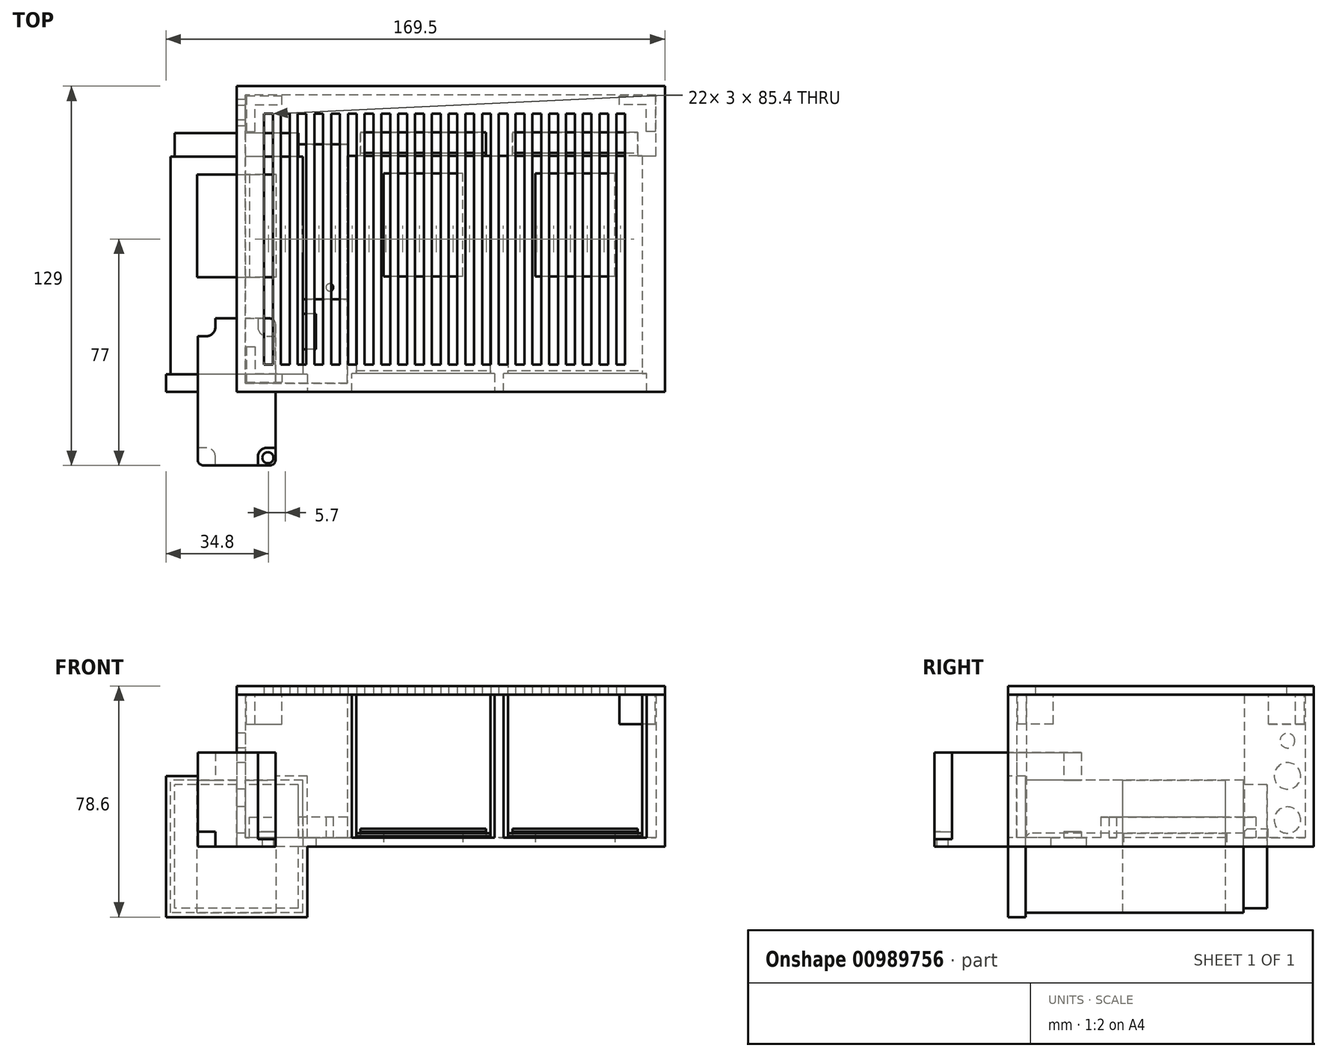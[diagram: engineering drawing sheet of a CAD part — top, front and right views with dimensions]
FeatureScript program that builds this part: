
annotation { "Feature Type Name" : "Feature", "Feature Type Description" : "" }
export const myFeature = defineFeature(function(context is Context, id is Id, definition is map)
    precondition{}
    {
        {
            assignVariable(context, id + "F0", {"name" : "panel_width", "anyValue" : 48 * mm});
        }
        {
            assignVariable(context, id + "F1", {"name" : "panel_depth", "anyValue" : 6 * mm});
        }
        {
            assignVariable(context, id + "F2", {"name" : "body_width", "anyValue" : 45 * mm});
        }
        {
            assignVariable(context, id + "F3", {"name" : "body_depth", "anyValue" : 74 * mm});
        }
        {
            assignVariable(context, id + "F4", {"name" : "connector_width", "anyValue" : 42 * mm});
        }
        {
            assignVariable(context, id + "F5", {"name" : "connector_depth", "anyValue" : 8 * mm});
        }
        {
            assignVariable(context, id + "F6", {"name" : "tol", "anyValue" : 0.3 * mm});
        }
        {
            assignVariable(context, id + "F7", {"name" : "eltako_height", "anyValue" : 32 * mm});
        }
        {
            assignVariable(context, id + "F8", {"name" : "eltako_h1", "anyValue" : 2.5 * mm});
        }
        {
            assignVariable(context, id + "F9", {"name" : "eltako_h2", "anyValue" : 5 * mm});
        }
        {
            assignVariable(context, id + "F10", {"name" : "wt", "anyValue" : 3 * mm});
        }
        {
            var Q0;
            Q0=qCreatedBy(makeId("Front.planeOp"),FACE);
            var sketch = newSketch(context, id + "F11", { "sketchPlane" : qUnion([Q0])});
            skLineSegment(sketch, "E0.bottom", {"start": v(24, -24) * mm, "end": v(-24, -24) * mm});
            skLineSegment(sketch, "E0.top", {"start": v(24, 24) * mm, "end": v(-24, 24) * mm});
            skLineSegment(sketch, "E0.left", {"start": v(24, -24) * mm, "end": v(24, 24) * mm});
            skLineSegment(sketch, "E0.right", {"start": v(-24, -24) * mm, "end": v(-24, 24) * mm});
            skPoint(sketch, "E0.middle", {"position": v(0, 0) * mm});
            skLineSegment(sketch, "E1.bottom", {"start": v(22.5, -22.5) * mm, "end": v(-22.5, -22.5) * mm});
            skLineSegment(sketch, "E1.top", {"start": v(22.5, 22.5) * mm, "end": v(-22.5, 22.5) * mm});
            skLineSegment(sketch, "E1.left", {"start": v(22.5, -22.5) * mm, "end": v(22.5, 22.5) * mm});
            skLineSegment(sketch, "E1.right", {"start": v(-22.5, -22.5) * mm, "end": v(-22.5, 22.5) * mm});
            skLineSegment(sketch, "E2.bottom", {"start": v(21, -21) * mm, "end": v(-21, -21) * mm});
            skLineSegment(sketch, "E2.top", {"start": v(21, 21) * mm, "end": v(-21, 21) * mm});
            skLineSegment(sketch, "E2.left", {"start": v(21, -21) * mm, "end": v(21, 21) * mm});
            skLineSegment(sketch, "E2.right", {"start": v(-21, -21) * mm, "end": v(-21, 21) * mm});
            skSolve(sketch);
        }
        {
            var Q0;
            Q0=makeQuery(id+"F11.imprint","IMPRINT",FACE,{"disambiguationData":[TD([[makeQuery(id+"F11.imprint","IMPRINT",EDGE,{"derivedFrom":sQuery(id+"F11.wireOp",EDGE,"E2.bottom")}),-1.0]])]});
            extrude(context, id + "F12", {"entities" : qUnion([Q0]), "oppositeDirection" : true, "depth" : getVariable(context, 'panel_depth') + getVariable(context, 'body_depth') + getVariable(context, 'connector_depth'), "offsetDistance" : 25 * mm});
        }
        {
            var Q0;
            Q0=makeQuery(id+"F11.imprint","IMPRINT",FACE,{"disambiguationData":[TD([[makeQuery(id+"F11.imprint","IMPRINT",EDGE,{"derivedFrom":sQuery(id+"F11.wireOp",EDGE,"E1.bottom")}),-1.0]])]});
            extrude(context, id + "F13", {"entities" : qUnion([Q0]), "operationType" : NewBodyOperationType.ADD, "oppositeDirection" : true, "depth" : getVariable(context, 'panel_depth') + getVariable(context, 'body_depth'), "offsetDistance" : 25 * mm});
        }
        {
            var Q0;
            Q0=makeQuery(id+"F11.imprint","IMPRINT",FACE,{"disambiguationData":[TD([[makeQuery(id+"F11.imprint","IMPRINT",EDGE,{"derivedFrom":sQuery(id+"F11.wireOp",EDGE,"E0.bottom")}),-1.0]])]});
            extrude(context, id + "F14", {"entities" : qUnion([Q0]), "operationType" : NewBodyOperationType.ADD, "oppositeDirection" : true, "depth" : getVariable(context, 'panel_depth'), "offsetDistance" : 25 * mm});
        }
        {
            var Q0;
            Q0=makeQuery(id+"F13.opExtrude","SWEPT_FACE",FACE,{"disambiguationData":[OSD([sQuery(id+"F11.wireOp",EDGE,"E1.top")])]});
            var sketch = newSketch(context, id + "F15", { "sketchPlane" : qUnion([Q0])});
            skLineSegment(sketch, "E3.bottom", {"start": v(13.5, 39) * mm, "end": v(-13.5, 39) * mm});
            skLineSegment(sketch, "E3.top", {"start": v(13.5, 74) * mm, "end": v(-13.5, 74) * mm});
            skLineSegment(sketch, "E3.left", {"start": v(13.5, 39) * mm, "end": v(13.5, 74) * mm});
            skLineSegment(sketch, "E3.right", {"start": v(-13.5, 39) * mm, "end": v(-13.5, 74) * mm});
            skPoint(sketch, "E3.middle", {"position": v(0, 56.5) * mm});
            skSolve(sketch);
        }
        {
            var Q0;
            Q0=makeQuery(id+"F15.imprint","IMPRINT",FACE,{"disambiguationData":[TD([[makeQuery(id+"F15.imprint","IMPRINT",EDGE,{"derivedFrom":sQuery(id+"F15.wireOp",EDGE,"E3.bottom")}),-1.0]])]});
            var Q1;
            Q1=makeQuery(id+"F13.opExtrude","SWEPT_FACE",FACE,{"disambiguationData":[OSD([sQuery(id+"F11.wireOp",EDGE,"E1.bottom")])]});
            extrude(context, id + "F16", {"entities" : qUnion([Q0]), "operationType" : NewBodyOperationType.REMOVE, "endBound" : BoundingType.UP_TO_SURFACE, "oppositeDirection" : true, "depth" : 25 * mm, "endBoundEntityFace" : qUnion([Q1]), "offsetDistance" : 25 * mm});
        }
        {
            var Q0;
            Q0=qCreatedBy(makeId("Top.planeOp"),FACE);
            var sketch = newSketch(context, id + "F17", { "sketchPlane" : qUnion([Q0])});
            skLineSegment(sketch, "E4.bottom", {"start": v(11.25, -25) * mm, "end": v(-11.25, -25) * mm});
            skLineSegment(sketch, "E4.top", {"start": v(11.25, 25) * mm, "end": v(-11.25, 25) * mm});
            skLineSegment(sketch, "E4.left", {"start": v(13.25, -23) * mm, "end": v(13.25, 23) * mm});
            skLineSegment(sketch, "E4.right", {"start": v(-13.25, -23) * mm, "end": v(-13.25, 23) * mm});
            skPoint(sketch, "E4.middle", {"position": v(0, 0) * mm});
            skPoint(sketch, "E5.visualSharp", {"position": v(13.25, 25) * mm});
            skArc(sketch, "E5.filletArc", {"start": v(13.25, 23) * mm, "mid": v(12.66, 24.41) * mm, "end": v(11.25, 25) * mm});
            skPoint(sketch, "E6.visualSharp", {"position": v(13.25, -25) * mm});
            skArc(sketch, "E6.filletArc", {"start": v(11.25, -25) * mm, "mid": v(12.66, -24.41) * mm, "end": v(13.25, -23) * mm});
            skPoint(sketch, "E7.visualSharp", {"position": v(-13.25, -25) * mm});
            skArc(sketch, "E7.filletArc", {"start": v(-13.25, -23) * mm, "mid": v(-12.66, -24.41) * mm, "end": v(-11.25, -25) * mm});
            skPoint(sketch, "E8.visualSharp", {"position": v(-13.25, 25) * mm});
            skArc(sketch, "E8.filletArc", {"start": v(-11.25, 25) * mm, "mid": v(-12.66, 24.41) * mm, "end": v(-13.25, 23) * mm});
            skLineSegment(sketch, "E9", {"start": v(7.25, 25) * mm, "end": v(7.25, 22) * mm});
            skLineSegment(sketch, "E10", {"start": v(10.25, 19) * mm, "end": v(13.25, 19) * mm});
            skPoint(sketch, "E11.visualSharp", {"position": v(7.25, 19) * mm});
            skArc(sketch, "E11.filletArc", {"start": v(7.25, 22) * mm, "mid": v(8.13, 19.88) * mm, "end": v(10.25, 19) * mm});
            skLineSegment(sketch, "E12", {"start": v(-13.25, 0) * mm, "end": v(13.25, 0) * mm, "construction": true});
            skLineSegment(sketch, "E13", {"start": v(0, 25) * mm, "end": v(0, -25) * mm, "construction": true});
            skLineSegment(sketch, "E14.MirrorCS", {"start": v(-7.25, 25) * mm, "end": v(-7.25, 22) * mm});
            skArc(sketch, "E15.MirrorCS", {"start": v(-7.25, 22) * mm, "mid": v(-8.13, 19.88) * mm, "end": v(-10.25, 19) * mm});
            skLineSegment(sketch, "E16.MirrorCS", {"start": v(-10.25, 19) * mm, "end": v(-13.25, 19) * mm});
            skLineSegment(sketch, "E17.MirrorCS", {"start": v(-10.25, -19) * mm, "end": v(-13.25, -19) * mm});
            skArc(sketch, "E18.MirrorCS", {"start": v(-7.25, -22) * mm, "mid": v(-8.13, -19.88) * mm, "end": v(-10.25, -19) * mm});
            skLineSegment(sketch, "E19.MirrorCS", {"start": v(-7.25, -25) * mm, "end": v(-7.25, -22) * mm});
            skLineSegment(sketch, "E20.MirrorCS", {"start": v(7.25, -25) * mm, "end": v(7.25, -22) * mm});
            skArc(sketch, "E21.MirrorCS", {"start": v(7.25, -22) * mm, "mid": v(8.13, -19.88) * mm, "end": v(10.25, -19) * mm});
            skLineSegment(sketch, "E22.MirrorCS", {"start": v(10.25, -19) * mm, "end": v(13.25, -19) * mm});
            skCircle(sketch, "E23", {"center": v(10.61, -22.36) * mm, "radius": 1.9 * mm});
            skLineSegment(sketch, "E24", {"start": v(10.25, -22) * mm, "end": v(11.25, -23) * mm, "construction": true});
            skLineSegment(sketch, "E25", {"start": v(12.51, -22.36) * mm, "end": v(13.25, -22.36) * mm, "construction": true});
            skLineSegment(sketch, "E26", {"start": v(10.61, -24.26) * mm, "end": v(10.61, -25) * mm, "construction": true});
            skCircle(sketch, "E27.1.0", {"center": v(-10.61, 22.36) * mm, "radius": 1.9 * mm});
            skLineSegment(sketch, "E28", {"start": v(10.61, -22.36) * mm, "end": v(0, 0) * mm, "construction": true});
            skLineSegment(sketch, "E29", {"start": v(0, 0) * mm, "end": v(-10.61, 22.36) * mm, "construction": true});
            skLineSegment(sketch, "E30", {"start": v(-10.61, 22.36) * mm, "end": v(10.61, 22.36) * mm, "construction": true});
            skLineSegment(sketch, "E31", {"start": v(10.61, 22.36) * mm, "end": v(10.61, -22.36) * mm, "construction": true});
            skSolve(sketch);
        }
        {
            var Q0;
            {var subQ1=sQuery(id+"F17.wireOp",EDGE,"E5.filletArc");Q0=makeQuery(id+"F17.imprint","IMPRINT",FACE,{"disambiguationData":[TD([[makeQuery(id+"F17.imprint","IMPRINT",EDGE,{"derivedFrom":subQ1}),1.0]])]});}
            var Q1;
            {var subQ2=sQuery(id+"F17.wireOp",EDGE,"E9");Q1=makeQuery(id+"F17.imprint","IMPRINT",FACE,{"disambiguationData":[TD([[makeQuery(id+"F17.imprint","IMPRINT",EDGE,{"derivedFrom":subQ2}),-1.0]])]});}
            var Q2;
            {var subQ0=sQuery(id+"F17.wireOp",EDGE,"E7.filletArc");Q2=makeQuery(id+"F17.imprint","IMPRINT",FACE,{"disambiguationData":[TD([[makeQuery(id+"F17.imprint","IMPRINT",EDGE,{"derivedFrom":subQ0}),1.0]])]});}
            extrude(context, id + "F18", {"entities" : qUnion([Q0, Q1, Q2]), "depth" : getVariable(context, 'eltako_height'), "offsetDistance" : 25 * mm});
        }
        {
            var Q0;
            {var subQ0=sQuery(id+"F17.wireOp",EDGE,"E6.filletArc");Q0=makeQuery(id+"F17.imprint","IMPRINT",FACE,{"disambiguationData":[TD([[makeQuery(id+"F17.imprint","IMPRINT",EDGE,{"derivedFrom":subQ0}),1.0]])]});}
            var Q1;
            {var subQ1=sQuery(id+"F17.wireOp",EDGE,"E8.filletArc");Q1=makeQuery(id+"F17.imprint","IMPRINT",FACE,{"disambiguationData":[TD([[makeQuery(id+"F17.imprint","IMPRINT",EDGE,{"derivedFrom":subQ1}),1.0]])]});}
            extrude(context, id + "F19", {"entities" : qUnion([Q0, Q1]), "operationType" : NewBodyOperationType.ADD, "depth" : getVariable(context, 'eltako_h1'), "offsetDistance" : 25 * mm});
        }
        {
            var Q0;
            {var subQ1=sQuery(id+"F17.wireOp",EDGE,"E5.filletArc");Q0=makeQuery(id+"F17.imprint","IMPRINT",FACE,{"disambiguationData":[TD([[makeQuery(id+"F17.imprint","IMPRINT",EDGE,{"derivedFrom":subQ1}),1.0]])]});}
            var Q1;
            {var subQ0=sQuery(id+"F17.wireOp",EDGE,"E7.filletArc");Q1=makeQuery(id+"F17.imprint","IMPRINT",FACE,{"disambiguationData":[TD([[makeQuery(id+"F17.imprint","IMPRINT",EDGE,{"derivedFrom":subQ0}),1.0]])]});}
            extrude(context, id + "F20", {"entities" : qUnion([Q0, Q1]), "operationType" : NewBodyOperationType.REMOVE, "depth" : getVariable(context, 'eltako_h2'), "offsetDistance" : 25 * mm});
        }
        {
            var Q0;
            Q0=qCreatedBy(makeId("Top.planeOp"),FACE);
            var sketch = newSketch(context, id + "F21", { "sketchPlane" : qUnion([Q0])});
            skLineSegment(sketch, "E32", {"start": v(0, 0) * mm, "end": v(145.5, 0) * mm});
            skLineSegment(sketch, "E33", {"start": v(0, 0) * mm, "end": v(0, 104) * mm});
            skLineSegment(sketch, "E34", {"start": v(0, 104) * mm, "end": v(145.5, 104) * mm});
            skLineSegment(sketch, "E35", {"start": v(145.5, 104) * mm, "end": v(145.5, 0) * mm});
            skLineSegment(sketch, "E36.0", {"start": v(3, 101) * mm, "end": v(142.5, 101) * mm});
            skLineSegment(sketch, "E36.1", {"start": v(3, 3) * mm, "end": v(3, 101) * mm});
            skLineSegment(sketch, "E36.2", {"start": v(3, 3) * mm, "end": v(142.5, 3) * mm});
            skLineSegment(sketch, "E36.3", {"start": v(142.5, 101) * mm, "end": v(142.5, 3) * mm});
            skLineSegment(sketch, "E37", {"start": v(137.8, 80.3) * mm, "end": v(137.8, 6.3) * mm});
            skLineSegment(sketch, "E38", {"start": v(137.8, 6.3) * mm, "end": v(139.3, 6.3) * mm});
            skLineSegment(sketch, "E39", {"start": v(139.3, 6.3) * mm, "end": v(139.3, 0) * mm});
            skLineSegment(sketch, "E40", {"start": v(137.8, 80.3) * mm, "end": v(136.3, 80.3) * mm});
            skLineSegment(sketch, "E41", {"start": v(136.3, 80.3) * mm, "end": v(136.3, 88.3) * mm});
            skLineSegment(sketch, "E42", {"start": v(136.3, 88.3) * mm, "end": v(93.7, 88.3) * mm});
            skLineSegment(sketch, "E43", {"start": v(93.7, 88.3) * mm, "end": v(93.7, 80.3) * mm});
            skLineSegment(sketch, "E44", {"start": v(93.7, 80.3) * mm, "end": v(92.2, 80.3) * mm});
            skLineSegment(sketch, "E45", {"start": v(92.2, 80.3) * mm, "end": v(92.2, 6.3) * mm});
            skLineSegment(sketch, "E46", {"start": v(92.2, 6.3) * mm, "end": v(90.7, 6.3) * mm});
            skLineSegment(sketch, "E47", {"start": v(90.7, 6.3) * mm, "end": v(90.7, 0) * mm});
            skLineSegment(sketch, "E48", {"start": v(87.7, 0) * mm, "end": v(87.7, 6.3) * mm});
            skLineSegment(sketch, "E49", {"start": v(87.7, 6.3) * mm, "end": v(86.2, 6.3) * mm});
            skLineSegment(sketch, "E50", {"start": v(86.2, 6.3) * mm, "end": v(86.2, 80.3) * mm});
            skLineSegment(sketch, "E51", {"start": v(86.2, 80.3) * mm, "end": v(84.7, 80.3) * mm});
            skLineSegment(sketch, "E52", {"start": v(84.7, 80.3) * mm, "end": v(84.7, 88.3) * mm});
            skLineSegment(sketch, "E53", {"start": v(84.7, 88.3) * mm, "end": v(42.1, 88.3) * mm});
            skLineSegment(sketch, "E54", {"start": v(42.1, 88.3) * mm, "end": v(42.1, 80.3) * mm});
            skLineSegment(sketch, "E55", {"start": v(42.1, 80.3) * mm, "end": v(40.6, 80.3) * mm});
            skLineSegment(sketch, "E56", {"start": v(40.6, 80.3) * mm, "end": v(40.6, 6.3) * mm});
            skLineSegment(sketch, "E57", {"start": v(40.6, 6.3) * mm, "end": v(39.1, 6.3) * mm});
            skLineSegment(sketch, "E58", {"start": v(39.1, 6.3) * mm, "end": v(39.1, 0) * mm});
            skLineSegment(sketch, "E59", {"start": v(92.2, 6.3) * mm, "end": v(137.8, 6.3) * mm});
            skLineSegment(sketch, "E60", {"start": v(93.7, 80.3) * mm, "end": v(136.3, 80.3) * mm});
            skLineSegment(sketch, "E61", {"start": v(42.1, 80.3) * mm, "end": v(84.7, 80.3) * mm});
            skLineSegment(sketch, "E62", {"start": v(40.6, 6.3) * mm, "end": v(86.2, 6.3) * mm});
            skLineSegment(sketch, "E63.bottom", {"start": v(76.9, 39.3) * mm, "end": v(49.9, 39.3) * mm});
            skLineSegment(sketch, "E63.top", {"start": v(76.9, 74.3) * mm, "end": v(49.9, 74.3) * mm});
            skLineSegment(sketch, "E63.left", {"start": v(76.9, 39.3) * mm, "end": v(76.9, 74.3) * mm});
            skLineSegment(sketch, "E63.right", {"start": v(49.9, 39.3) * mm, "end": v(49.9, 74.3) * mm});
            skPoint(sketch, "E63.middle", {"position": v(63.4, 56.8) * mm});
            skLineSegment(sketch, "E64", {"start": v(63.4, 39.3) * mm, "end": v(63.4, 6.3) * mm, "construction": true});
            skLineSegment(sketch, "E65.bottom", {"start": v(128.5, 39.3) * mm, "end": v(101.5, 39.3) * mm});
            skLineSegment(sketch, "E65.top", {"start": v(128.5, 74.3) * mm, "end": v(101.5, 74.3) * mm});
            skLineSegment(sketch, "E65.left", {"start": v(128.5, 39.3) * mm, "end": v(128.5, 74.3) * mm});
            skLineSegment(sketch, "E65.right", {"start": v(101.5, 39.3) * mm, "end": v(101.5, 74.3) * mm});
            skPoint(sketch, "E65.middle", {"position": v(115, 56.8) * mm});
            skLineSegment(sketch, "E66", {"start": v(115, 39.3) * mm, "end": v(115, 6.3) * mm, "construction": true});
            skCircle(sketch, "E67", {"center": v(10.37, 80.3) * mm, "radius": 1.25 * mm});
            skCircle(sketch, "E68", {"center": v(31.6, 35.57) * mm, "radius": 1.25 * mm});
            skLineSegment(sketch, "E69", {"start": v(10.37, 80.3) * mm, "end": v(31.6, 80.3) * mm, "construction": true});
            skLineSegment(sketch, "E70", {"start": v(31.6, 80.3) * mm, "end": v(31.6, 35.57) * mm, "construction": true});
            skLineSegment(sketch, "E71.bottom", {"start": v(37.6, 31.57) * mm, "end": v(4.37, 31.57) * mm});
            skLineSegment(sketch, "E71.top", {"start": v(37.6, 84.3) * mm, "end": v(4.37, 84.3) * mm});
            skLineSegment(sketch, "E71.left", {"start": v(37.6, 31.57) * mm, "end": v(37.6, 84.3) * mm});
            skLineSegment(sketch, "E71.right", {"start": v(4.37, 31.57) * mm, "end": v(4.37, 84.3) * mm});
            skPoint(sketch, "E71.middle", {"position": v(20.99, 57.94) * mm});
            skLineSegment(sketch, "E72", {"start": v(20.99, 80.3) * mm, "end": v(20.99, 57.94) * mm, "construction": true});
            skLineSegment(sketch, "E73", {"start": v(20.99, 57.94) * mm, "end": v(31.6, 57.94) * mm, "construction": true});
            skLineSegment(sketch, "E74", {"start": v(37.6, 31.57) * mm, "end": v(37.6, 3) * mm});
            skLineSegment(sketch, "E75.bottom", {"start": v(26.99, 14.57) * mm, "end": v(14.99, 14.57) * mm});
            skLineSegment(sketch, "E75.top", {"start": v(26.99, 26.57) * mm, "end": v(14.99, 26.57) * mm});
            skLineSegment(sketch, "E75.left", {"start": v(26.99, 14.57) * mm, "end": v(26.99, 26.57) * mm});
            skLineSegment(sketch, "E75.right", {"start": v(14.99, 14.57) * mm, "end": v(14.99, 26.57) * mm});
            skPoint(sketch, "E75.middle", {"position": v(20.99, 20.57) * mm});
            skLineSegment(sketch, "E76", {"start": v(20.99, 26.57) * mm, "end": v(20.99, 31.57) * mm, "construction": true});
            skLineSegment(sketch, "E77", {"start": v(86.2, 80.3) * mm, "end": v(92.2, 80.3) * mm});
            skLineSegment(sketch, "E78", {"start": v(137.8, 80.3) * mm, "end": v(142.5, 80.3) * mm});
            skLineSegment(sketch, "E79", {"start": v(40.6, 80.3) * mm, "end": v(37.6, 80.3) * mm});
            skSolve(sketch);
        }
        {
            var Q0;
            Q0=makeQuery(id+"F21.imprint","IMPRINT",FACE,{"disambiguationData":[TD([[makeQuery(id+"F21.imprint","IMPRINT",EDGE,{"derivedFrom":sQuery(id+"F21.wireOp",EDGE,"E36.0")}),-1.0]])]});
            var Q1;
            Q1=makeQuery(id+"F21.imprint","IMPRINT",FACE,{"disambiguationData":[TD([[makeQuery(id+"F21.imprint","IMPRINT",EDGE,{"derivedFrom":sQuery(id+"F21.wireOp",EDGE,"E67")}),1.0]])]});
            var Q2;
            Q2=makeQuery(id+"F21.imprint","IMPRINT",FACE,{"disambiguationData":[TD([[makeQuery(id+"F21.imprint","IMPRINT",EDGE,{"derivedFrom":sQuery(id+"F21.wireOp",EDGE,"E68")}),1.0]])]});
            var Q3;
            Q3=makeQuery(id+"F21.imprint","IMPRINT",FACE,{"disambiguationData":[TD([[makeQuery(id+"F21.imprint","IMPRINT",EDGE,{"derivedFrom":sQuery(id+"F21.wireOp",EDGE,"E67")}),-1.0]])]});
            var Q4;
            Q4=makeQuery(id+"F21.imprint","IMPRINT",FACE,{"disambiguationData":[TD([[makeQuery(id+"F21.imprint","IMPRINT",EDGE,{"derivedFrom":sQuery(id+"F21.wireOp",EDGE,"E52")}),1.0]])]});
            var Q5;
            Q5=makeQuery(id+"F21.imprint","IMPRINT",FACE,{"disambiguationData":[TD([[makeQuery(id+"F21.imprint","IMPRINT",EDGE,{"derivedFrom":sQuery(id+"F21.wireOp",EDGE,"E50")}),1.0]])]});
            var Q6;
            {var subQ1=sQuery(id+"F21.wireOp",EDGE,"E49");Q6=makeQuery(id+"F21.imprint","IMPRINT",FACE,{"disambiguationData":[TD([[makeQuery(id+"F21.imprint","IMPRINT",EDGE,{"derivedFrom":subQ1}),1.0]])]});}
            var Q7;
            {var subQ1=sQuery(id+"F21.wireOp",EDGE,"E38");Q7=makeQuery(id+"F21.imprint","IMPRINT",FACE,{"disambiguationData":[TD([[makeQuery(id+"F21.imprint","IMPRINT",EDGE,{"derivedFrom":subQ1}),-1.0]])]});}
            var Q8;
            Q8=makeQuery(id+"F21.imprint","IMPRINT",FACE,{"disambiguationData":[TD([[makeQuery(id+"F21.imprint","IMPRINT",EDGE,{"derivedFrom":sQuery(id+"F21.wireOp",EDGE,"E37")}),-1.0]])]});
            var Q9;
            Q9=makeQuery(id+"F21.imprint","IMPRINT",FACE,{"disambiguationData":[TD([[makeQuery(id+"F21.imprint","IMPRINT",EDGE,{"derivedFrom":sQuery(id+"F21.wireOp",EDGE,"E41")}),1.0]])]});
            var Q10;
            {var subQ8=sQuery(id+"F21.wireOp",EDGE,"E33");Q10=makeQuery(id+"F21.imprint","IMPRINT",FACE,{"disambiguationData":[TD([[makeQuery(id+"F21.imprint","IMPRINT",EDGE,{"derivedFrom":subQ8}),-1.0]])]});}
            var Q11;
            {var subQ0=sQuery(id+"F21.wireOp",EDGE,"E47");var subQ1=sQuery(id+"F21.wireOp",EDGE,"E32");var subQ2=makeQuery(id+"F21.imprint","INTERSECT",VERTEX,{"derivedFrom":[subQ1,subQ0]});Q11=makeQuery(id+"F21.imprint","IMPRINT",FACE,{"disambiguationData":[TD([[makeQuery(id+"F21.imprint","IMPRINT",EDGE,{"disambiguationData":[TD([[subQ2,1.0]])],"derivedFrom":subQ1}),1.0]])]});}
            var Q12;
            {var subQ0=sQuery(id+"F21.wireOp",EDGE,"E48");var subQ1=sQuery(id+"F21.wireOp",EDGE,"E32");var subQ2=makeQuery(id+"F21.imprint","INTERSECT",VERTEX,{"derivedFrom":[subQ1,subQ0]});Q12=makeQuery(id+"F21.imprint","IMPRINT",FACE,{"disambiguationData":[TD([[makeQuery(id+"F21.imprint","IMPRINT",EDGE,{"disambiguationData":[TD([[subQ2,1.0]])],"derivedFrom":subQ1}),1.0]])]});}
            var Q13;
            {var subQ0=sQuery(id+"F21.wireOp",EDGE,"E39");var subQ1=sQuery(id+"F21.wireOp",EDGE,"E32");var subQ2=makeQuery(id+"F21.imprint","INTERSECT",VERTEX,{"derivedFrom":[subQ1,subQ0]});Q13=makeQuery(id+"F21.imprint","IMPRINT",FACE,{"disambiguationData":[TD([[makeQuery(id+"F21.imprint","IMPRINT",EDGE,{"disambiguationData":[TD([[subQ2,1.0]])],"derivedFrom":subQ1}),1.0]])]});}
            var Q14;
            Q14=makeQuery(id+"F21.imprint","IMPRINT",FACE,{"disambiguationData":[TD([[makeQuery(id+"F21.imprint","IMPRINT",EDGE,{"derivedFrom":sQuery(id+"F21.wireOp",EDGE,"E54")}),-1.0]])]});
            var Q15;
            Q15=makeQuery(id+"F21.imprint","IMPRINT",FACE,{"disambiguationData":[TD([[makeQuery(id+"F21.imprint","IMPRINT",EDGE,{"derivedFrom":sQuery(id+"F21.wireOp",EDGE,"E43")}),-1.0]])]});
            var Q16;
            Q16=makeQuery(id+"F21.imprint","IMPRINT",FACE,{"disambiguationData":[TD([[makeQuery(id+"F21.imprint","IMPRINT",EDGE,{"derivedFrom":sQuery(id+"F21.wireOp",EDGE,"E37")}),1.0]])]});
            var Q17;
            Q17=makeQuery(id+"F21.imprint","IMPRINT",FACE,{"disambiguationData":[TD([[makeQuery(id+"F21.imprint","IMPRINT",EDGE,{"derivedFrom":sQuery(id+"F21.wireOp",EDGE,"E56")}),-1.0]])]});
            var Q18;
            Q18=makeQuery(id+"F21.imprint","IMPRINT",FACE,{"disambiguationData":[TD([[makeQuery(id+"F21.imprint","IMPRINT",EDGE,{"derivedFrom":sQuery(id+"F21.wireOp",EDGE,"E45")}),-1.0]])]});
            extrude(context, id + "F22", {"entities" : qUnion([Q0, Q1, Q2, Q3, Q4, Q5, Q6, Q7, Q8, Q9, Q10, Q11, Q12, Q13, Q14, Q15, Q16, Q17, Q18]), "depth" : getVariable(context, 'wt'), "offsetDistance" : 25 * mm});
        }
        {
            var Q0;
            Q0=makeQuery(id+"F21.imprint","IMPRINT",FACE,{"disambiguationData":[TD([[makeQuery(id+"F21.imprint","IMPRINT",EDGE,{"derivedFrom":sQuery(id+"F21.wireOp",EDGE,"E67")}),-1.0]])]});
            extrude(context, id + "F23", {"entities" : qUnion([Q0]), "operationType" : NewBodyOperationType.ADD, "depth" : 10 * mm, "offsetDistance" : 25 * mm});
        }
        {
            var Q0;
            Q0=makeQuery(id+"F21.imprint","IMPRINT",FACE,{"disambiguationData":[TD([[makeQuery(id+"F21.imprint","IMPRINT",EDGE,{"derivedFrom":sQuery(id+"F21.wireOp",EDGE,"E50")}),1.0]])]});
            var Q1;
            Q1=makeQuery(id+"F21.imprint","IMPRINT",FACE,{"disambiguationData":[TD([[makeQuery(id+"F21.imprint","IMPRINT",EDGE,{"derivedFrom":sQuery(id+"F21.wireOp",EDGE,"E37")}),-1.0]])]});
            extrude(context, id + "F24", {"entities" : qUnion([Q0, Q1]), "operationType" : NewBodyOperationType.ADD, "depth" : getVariable(context, 'wt') + (getVariable(context, 'panel_width') - getVariable(context, 'body_width')) / 2, "offsetDistance" : 25 * mm});
        }
        {
            var Q0;
            Q0=makeQuery(id+"F21.imprint","IMPRINT",FACE,{"disambiguationData":[TD([[makeQuery(id+"F21.imprint","IMPRINT",EDGE,{"derivedFrom":sQuery(id+"F21.wireOp",EDGE,"E52")}),1.0]])]});
            var Q1;
            Q1=makeQuery(id+"F21.imprint","IMPRINT",FACE,{"disambiguationData":[TD([[makeQuery(id+"F21.imprint","IMPRINT",EDGE,{"derivedFrom":sQuery(id+"F21.wireOp",EDGE,"E41")}),1.0]])]});
            extrude(context, id + "F25", {"entities" : qUnion([Q0, Q1]), "operationType" : NewBodyOperationType.ADD, "depth" : getVariable(context, 'wt') + (getVariable(context, 'panel_width') - getVariable(context, 'connector_width')) / 2, "offsetDistance" : 25 * mm});
        }
        {
            var Q0;
            Q0=makeQuery(id+"F25.opExtrude","CAP_EDGE",EDGE,{"disambiguationData":[OSD([sQuery(id+"F21.wireOp",EDGE,"E61")])],"isStart":false});
            var Q1;
            Q1=makeQuery(id+"F25.opExtrude","CAP_EDGE",EDGE,{"disambiguationData":[OSD([sQuery(id+"F21.wireOp",EDGE,"E60")])],"isStart":false});
            var Q2;
            Q2=makeQuery(id+"F24.opExtrude","CAP_EDGE",EDGE,{"disambiguationData":[OSD([sQuery(id+"F21.wireOp",EDGE,"E62")])],"isStart":false});
            var Q3;
            Q3=makeQuery(id+"F24.opExtrude","CAP_EDGE",EDGE,{"disambiguationData":[OSD([sQuery(id+"F21.wireOp",EDGE,"E59")])],"isStart":false});
            chamfer(context, id + "F26", {"entities" : qUnion([Q0, Q1, Q2, Q3]), "width" : 1 * mm, "tangentPropagation" : true});
        }
        {
            var Q0;
            {var subQ7=sQuery(id+"F21.wireOp",EDGE,"E33");Q0=makeQuery(id+"F21.imprint","IMPRINT",FACE,{"disambiguationData":[TD([[makeQuery(id+"F21.imprint","IMPRINT",EDGE,{"derivedFrom":subQ7}),-1.0]])]});}
            var Q1;
            {var subQ0=sQuery(id+"F21.wireOp",EDGE,"E47");var subQ1=sQuery(id+"F21.wireOp",EDGE,"E32");var subQ2=makeQuery(id+"F21.imprint","INTERSECT",VERTEX,{"derivedFrom":[subQ1,subQ0]});Q1=makeQuery(id+"F21.imprint","IMPRINT",FACE,{"disambiguationData":[TD([[makeQuery(id+"F21.imprint","IMPRINT",EDGE,{"disambiguationData":[TD([[subQ2,1.0]])],"derivedFrom":subQ1}),1.0]])]});}
            var Q2;
            Q2=makeQuery(id+"F21.imprint","IMPRINT",FACE,{"disambiguationData":[TD([[makeQuery(id+"F21.imprint","IMPRINT",EDGE,{"derivedFrom":sQuery(id+"F21.wireOp",EDGE,"E37")}),1.0]])]});
            var Q3;
            Q3=makeQuery(id+"F21.imprint","IMPRINT",FACE,{"disambiguationData":[TD([[makeQuery(id+"F21.imprint","IMPRINT",EDGE,{"derivedFrom":sQuery(id+"F21.wireOp",EDGE,"E45")}),-1.0]])]});
            var Q4;
            Q4=makeQuery(id+"F21.imprint","IMPRINT",FACE,{"disambiguationData":[TD([[makeQuery(id+"F21.imprint","IMPRINT",EDGE,{"derivedFrom":sQuery(id+"F21.wireOp",EDGE,"E56")}),-1.0]])]});
            extrude(context, id + "F27", {"entities" : qUnion([Q0, Q1, Q2, Q3, Q4]), "operationType" : NewBodyOperationType.ADD, "depth" : getVariable(context, 'panel_width') + getVariable(context, 'wt') + 2 * getVariable(context, 'tol'), "offsetDistance" : 25 * mm});
        }
        {
            var Q0;
            Q0=makeQuery(id+"F27.opExtrude","CAP_FACE",FACE,{"disambiguationData":[OSD([sQuery(id+"F21.wireOp",EDGE,"E32"),sQuery(id+"F21.wireOp",EDGE,"E33"),sQuery(id+"F21.wireOp",EDGE,"E34"),sQuery(id+"F21.wireOp",EDGE,"E35"),sQuery(id+"F21.wireOp",EDGE,"E36.0"),sQuery(id+"F21.wireOp",EDGE,"E36.1"),sQuery(id+"F21.wireOp",EDGE,"E36.2"),sQuery(id+"F21.wireOp",EDGE,"E36.3"),sQuery(id+"F21.wireOp",EDGE,"E37"),sQuery(id+"F21.wireOp",EDGE,"E38"),sQuery(id+"F21.wireOp",EDGE,"E39"),sQuery(id+"F21.wireOp",EDGE,"E40"),sQuery(id+"F21.wireOp",EDGE,"E41"),sQuery(id+"F21.wireOp",EDGE,"E54"),sQuery(id+"F21.wireOp",EDGE,"E55"),sQuery(id+"F21.wireOp",EDGE,"E56"),sQuery(id+"F21.wireOp",EDGE,"E57"),sQuery(id+"F21.wireOp",EDGE,"E58"),sQuery(id+"F21.wireOp",EDGE,"E71.left"),sQuery(id+"F21.wireOp",EDGE,"xd7r32YJ-M1g8-MA27-Vl9j-4uMu6q0P4ttY"),sQuery(id+"F21.wireOp",EDGE,"jehwoo4C-V18V-R3hG-mfAo-VqdSc3Xi8J4A"),sQuery(id+"F21.wireOp",EDGE,"E74")])],"isStart":false});
            var sketch = newSketch(context, id + "F28", { "sketchPlane" : qUnion([Q0])});
            skLineSegment(sketch, "E80.bottom", {"start": v(145.5, 0) * mm, "end": v(0, 0) * mm});
            skLineSegment(sketch, "E80.top", {"start": v(145.5, 104) * mm, "end": v(0, 104) * mm});
            skLineSegment(sketch, "E80.left", {"start": v(145.5, 0) * mm, "end": v(145.5, 104) * mm});
            skLineSegment(sketch, "E80.right", {"start": v(0, 0) * mm, "end": v(0, 104) * mm});
            skPoint(sketch, "E80.middle", {"position": v(72.75, 52) * mm});
            skLineSegment(sketch, "E81.bottom", {"start": v(3.3, 100.7) * mm, "end": v(142.2, 100.7) * mm});
            skLineSegment(sketch, "E81.top", {"start": v(3.3, 3.3) * mm, "end": v(142.2, 3.3) * mm});
            skLineSegment(sketch, "E81.left", {"start": v(3.3, 100.7) * mm, "end": v(3.3, 3.3) * mm});
            skLineSegment(sketch, "E81.right", {"start": v(142.2, 100.7) * mm, "end": v(142.2, 3.3) * mm});
            skLineSegment(sketch, "E82", {"start": v(142.2, 88.6) * mm, "end": v(139.2, 88.6) * mm});
            skLineSegment(sketch, "E83", {"start": v(139.2, 88.6) * mm, "end": v(139.2, 97.7) * mm});
            skLineSegment(sketch, "E84", {"start": v(139.2, 97.7) * mm, "end": v(130.1, 97.7) * mm});
            skLineSegment(sketch, "E85", {"start": v(130.1, 97.7) * mm, "end": v(130.1, 100.7) * mm});
            skLineSegment(sketch, "E86", {"start": v(3.3, 15.4) * mm, "end": v(6.3, 15.4) * mm});
            skLineSegment(sketch, "E87", {"start": v(6.3, 15.4) * mm, "end": v(6.3, 6.3) * mm});
            skLineSegment(sketch, "E88", {"start": v(6.3, 6.3) * mm, "end": v(15.4, 6.3) * mm});
            skLineSegment(sketch, "E89", {"start": v(15.4, 6.3) * mm, "end": v(15.4, 3.3) * mm});
            skLineSegment(sketch, "E90", {"start": v(3.3, 88.6) * mm, "end": v(6.3, 88.6) * mm});
            skLineSegment(sketch, "E91", {"start": v(6.3, 88.6) * mm, "end": v(6.3, 97.7) * mm});
            skLineSegment(sketch, "E92", {"start": v(6.3, 97.7) * mm, "end": v(15.4, 97.7) * mm});
            skLineSegment(sketch, "E93", {"start": v(15.4, 97.7) * mm, "end": v(15.4, 100.7) * mm});
            skLineSegment(sketch, "E94.bottom", {"start": v(12.3, 9.3) * mm, "end": v(9.3, 9.3) * mm});
            skLineSegment(sketch, "E94.top", {"start": v(12.3, 94.7) * mm, "end": v(9.3, 94.7) * mm});
            skLineSegment(sketch, "E94.left", {"start": v(12.3, 9.3) * mm, "end": v(12.3, 94.7) * mm});
            skLineSegment(sketch, "E94.right", {"start": v(9.3, 9.3) * mm, "end": v(9.3, 94.7) * mm});
            skPoint(sketch, "E94.middle", {"position": v(10.8, 52) * mm});
            skLineSegment(sketch, "E95.1.0.0", {"start": v(18, 9.3) * mm, "end": v(18, 94.7) * mm});
            skLineSegment(sketch, "E95.1.0.1", {"start": v(18, 94.7) * mm, "end": v(15, 94.7) * mm});
            skLineSegment(sketch, "E95.1.0.2", {"start": v(15, 9.3) * mm, "end": v(15, 94.7) * mm});
            skLineSegment(sketch, "E95.1.0.3", {"start": v(18, 9.3) * mm, "end": v(15, 9.3) * mm});
            skLineSegment(sketch, "E95.2.0.0", {"start": v(23.7, 9.3) * mm, "end": v(23.7, 94.7) * mm});
            skLineSegment(sketch, "E95.2.0.1", {"start": v(23.7, 94.7) * mm, "end": v(20.7, 94.7) * mm});
            skLineSegment(sketch, "E95.2.0.2", {"start": v(20.7, 9.3) * mm, "end": v(20.7, 94.7) * mm});
            skLineSegment(sketch, "E95.2.0.3", {"start": v(23.7, 9.3) * mm, "end": v(20.7, 9.3) * mm});
            skLineSegment(sketch, "E95.3.0.0", {"start": v(29.4, 9.3) * mm, "end": v(29.4, 94.7) * mm});
            skLineSegment(sketch, "E95.3.0.1", {"start": v(29.4, 94.7) * mm, "end": v(26.4, 94.7) * mm});
            skLineSegment(sketch, "E95.3.0.2", {"start": v(26.4, 9.3) * mm, "end": v(26.4, 94.7) * mm});
            skLineSegment(sketch, "E95.3.0.3", {"start": v(29.4, 9.3) * mm, "end": v(26.4, 9.3) * mm});
            skLineSegment(sketch, "E95.4.0.0", {"start": v(35.1, 9.3) * mm, "end": v(35.1, 94.7) * mm});
            skLineSegment(sketch, "E95.4.0.1", {"start": v(35.1, 94.7) * mm, "end": v(32.1, 94.7) * mm});
            skLineSegment(sketch, "E95.4.0.2", {"start": v(32.1, 9.3) * mm, "end": v(32.1, 94.7) * mm});
            skLineSegment(sketch, "E95.4.0.3", {"start": v(35.1, 9.3) * mm, "end": v(32.1, 9.3) * mm});
            skLineSegment(sketch, "E95.5.0.0", {"start": v(40.8, 9.3) * mm, "end": v(40.8, 94.7) * mm});
            skLineSegment(sketch, "E95.5.0.1", {"start": v(40.8, 94.7) * mm, "end": v(37.8, 94.7) * mm});
            skLineSegment(sketch, "E95.5.0.2", {"start": v(37.8, 9.3) * mm, "end": v(37.8, 94.7) * mm});
            skLineSegment(sketch, "E95.5.0.3", {"start": v(40.8, 9.3) * mm, "end": v(37.8, 9.3) * mm});
            skLineSegment(sketch, "E95.6.0.0", {"start": v(46.5, 9.3) * mm, "end": v(46.5, 94.7) * mm});
            skLineSegment(sketch, "E95.6.0.1", {"start": v(46.5, 94.7) * mm, "end": v(43.5, 94.7) * mm});
            skLineSegment(sketch, "E95.6.0.2", {"start": v(43.5, 9.3) * mm, "end": v(43.5, 94.7) * mm});
            skLineSegment(sketch, "E95.6.0.3", {"start": v(46.5, 9.3) * mm, "end": v(43.5, 9.3) * mm});
            skLineSegment(sketch, "E95.7.0.0", {"start": v(52.2, 9.3) * mm, "end": v(52.2, 94.7) * mm});
            skLineSegment(sketch, "E95.7.0.1", {"start": v(52.2, 94.7) * mm, "end": v(49.2, 94.7) * mm});
            skLineSegment(sketch, "E95.7.0.2", {"start": v(49.2, 9.3) * mm, "end": v(49.2, 94.7) * mm});
            skLineSegment(sketch, "E95.7.0.3", {"start": v(52.2, 9.3) * mm, "end": v(49.2, 9.3) * mm});
            skLineSegment(sketch, "E95.8.0.0", {"start": v(57.9, 9.3) * mm, "end": v(57.9, 94.7) * mm});
            skLineSegment(sketch, "E95.8.0.1", {"start": v(57.9, 94.7) * mm, "end": v(54.9, 94.7) * mm});
            skLineSegment(sketch, "E95.8.0.2", {"start": v(54.9, 9.3) * mm, "end": v(54.9, 94.7) * mm});
            skLineSegment(sketch, "E95.8.0.3", {"start": v(57.9, 9.3) * mm, "end": v(54.9, 9.3) * mm});
            skLineSegment(sketch, "E95.9.0.0", {"start": v(63.6, 9.3) * mm, "end": v(63.6, 94.7) * mm});
            skLineSegment(sketch, "E95.9.0.1", {"start": v(63.6, 94.7) * mm, "end": v(60.6, 94.7) * mm});
            skLineSegment(sketch, "E95.9.0.2", {"start": v(60.6, 9.3) * mm, "end": v(60.6, 94.7) * mm});
            skLineSegment(sketch, "E95.9.0.3", {"start": v(63.6, 9.3) * mm, "end": v(60.6, 9.3) * mm});
            skLineSegment(sketch, "E95.10.0.0", {"start": v(69.3, 9.3) * mm, "end": v(69.3, 94.7) * mm});
            skLineSegment(sketch, "E95.10.0.1", {"start": v(69.3, 94.7) * mm, "end": v(66.3, 94.7) * mm});
            skLineSegment(sketch, "E95.10.0.2", {"start": v(66.3, 9.3) * mm, "end": v(66.3, 94.7) * mm});
            skLineSegment(sketch, "E95.10.0.3", {"start": v(69.3, 9.3) * mm, "end": v(66.3, 9.3) * mm});
            skLineSegment(sketch, "E95.11.0.0", {"start": v(75, 9.3) * mm, "end": v(75, 94.7) * mm});
            skLineSegment(sketch, "E95.11.0.1", {"start": v(75, 94.7) * mm, "end": v(72, 94.7) * mm});
            skLineSegment(sketch, "E95.11.0.2", {"start": v(72, 9.3) * mm, "end": v(72, 94.7) * mm});
            skLineSegment(sketch, "E95.11.0.3", {"start": v(75, 9.3) * mm, "end": v(72, 9.3) * mm});
            skLineSegment(sketch, "E95.12.0.0", {"start": v(80.7, 9.3) * mm, "end": v(80.7, 94.7) * mm});
            skLineSegment(sketch, "E95.12.0.1", {"start": v(80.7, 94.7) * mm, "end": v(77.7, 94.7) * mm});
            skLineSegment(sketch, "E95.12.0.2", {"start": v(77.7, 9.3) * mm, "end": v(77.7, 94.7) * mm});
            skLineSegment(sketch, "E95.12.0.3", {"start": v(80.7, 9.3) * mm, "end": v(77.7, 9.3) * mm});
            skLineSegment(sketch, "E95.13.0.0", {"start": v(86.4, 9.3) * mm, "end": v(86.4, 94.7) * mm});
            skLineSegment(sketch, "E95.13.0.1", {"start": v(86.4, 94.7) * mm, "end": v(83.4, 94.7) * mm});
            skLineSegment(sketch, "E95.13.0.2", {"start": v(83.4, 9.3) * mm, "end": v(83.4, 94.7) * mm});
            skLineSegment(sketch, "E95.13.0.3", {"start": v(86.4, 9.3) * mm, "end": v(83.4, 9.3) * mm});
            skLineSegment(sketch, "E95.14.0.0", {"start": v(92.1, 9.3) * mm, "end": v(92.1, 94.7) * mm});
            skLineSegment(sketch, "E95.14.0.1", {"start": v(92.1, 94.7) * mm, "end": v(89.1, 94.7) * mm});
            skLineSegment(sketch, "E95.14.0.2", {"start": v(89.1, 9.3) * mm, "end": v(89.1, 94.7) * mm});
            skLineSegment(sketch, "E95.14.0.3", {"start": v(92.1, 9.3) * mm, "end": v(89.1, 9.3) * mm});
            skLineSegment(sketch, "E95.15.0.0", {"start": v(97.8, 9.3) * mm, "end": v(97.8, 94.7) * mm});
            skLineSegment(sketch, "E95.15.0.1", {"start": v(97.8, 94.7) * mm, "end": v(94.8, 94.7) * mm});
            skLineSegment(sketch, "E95.15.0.2", {"start": v(94.8, 9.3) * mm, "end": v(94.8, 94.7) * mm});
            skLineSegment(sketch, "E95.15.0.3", {"start": v(97.8, 9.3) * mm, "end": v(94.8, 9.3) * mm});
            skLineSegment(sketch, "E95.16.0.0", {"start": v(103.5, 9.3) * mm, "end": v(103.5, 94.7) * mm});
            skLineSegment(sketch, "E95.16.0.1", {"start": v(103.5, 94.7) * mm, "end": v(100.5, 94.7) * mm});
            skLineSegment(sketch, "E95.16.0.2", {"start": v(100.5, 9.3) * mm, "end": v(100.5, 94.7) * mm});
            skLineSegment(sketch, "E95.16.0.3", {"start": v(103.5, 9.3) * mm, "end": v(100.5, 9.3) * mm});
            skLineSegment(sketch, "E95.17.0.0", {"start": v(109.2, 9.3) * mm, "end": v(109.2, 94.7) * mm});
            skLineSegment(sketch, "E95.17.0.1", {"start": v(109.2, 94.7) * mm, "end": v(106.2, 94.7) * mm});
            skLineSegment(sketch, "E95.17.0.2", {"start": v(106.2, 9.3) * mm, "end": v(106.2, 94.7) * mm});
            skLineSegment(sketch, "E95.17.0.3", {"start": v(109.2, 9.3) * mm, "end": v(106.2, 9.3) * mm});
            skLineSegment(sketch, "E95.18.0.0", {"start": v(114.9, 9.3) * mm, "end": v(114.9, 94.7) * mm});
            skLineSegment(sketch, "E95.18.0.1", {"start": v(114.9, 94.7) * mm, "end": v(111.9, 94.7) * mm});
            skLineSegment(sketch, "E95.18.0.2", {"start": v(111.9, 9.3) * mm, "end": v(111.9, 94.7) * mm});
            skLineSegment(sketch, "E95.18.0.3", {"start": v(114.9, 9.3) * mm, "end": v(111.9, 9.3) * mm});
            skLineSegment(sketch, "E95.19.0.0", {"start": v(120.6, 9.3) * mm, "end": v(120.6, 94.7) * mm});
            skLineSegment(sketch, "E95.19.0.1", {"start": v(120.6, 94.7) * mm, "end": v(117.6, 94.7) * mm});
            skLineSegment(sketch, "E95.19.0.2", {"start": v(117.6, 9.3) * mm, "end": v(117.6, 94.7) * mm});
            skLineSegment(sketch, "E95.19.0.3", {"start": v(120.6, 9.3) * mm, "end": v(117.6, 9.3) * mm});
            skLineSegment(sketch, "E95.20.0.0", {"start": v(126.3, 9.3) * mm, "end": v(126.3, 94.7) * mm});
            skLineSegment(sketch, "E95.20.0.1", {"start": v(126.3, 94.7) * mm, "end": v(123.3, 94.7) * mm});
            skLineSegment(sketch, "E95.20.0.2", {"start": v(123.3, 9.3) * mm, "end": v(123.3, 94.7) * mm});
            skLineSegment(sketch, "E95.20.0.3", {"start": v(126.3, 9.3) * mm, "end": v(123.3, 9.3) * mm});
            skLineSegment(sketch, "E95.21.0.0", {"start": v(132, 9.3) * mm, "end": v(132, 94.7) * mm});
            skLineSegment(sketch, "E95.21.0.1", {"start": v(132, 94.7) * mm, "end": v(129, 94.7) * mm});
            skLineSegment(sketch, "E95.21.0.2", {"start": v(129, 9.3) * mm, "end": v(129, 94.7) * mm});
            skLineSegment(sketch, "E95.21.0.3", {"start": v(132, 9.3) * mm, "end": v(129, 9.3) * mm});
            skLineSegment(sketch, "E95.direction1", {"start": v(9.3, 9.3) * mm, "end": v(15, 9.3) * mm, "construction": true});
            skSolve(sketch);
        }
        {
            var Q0;
            Q0=makeQuery(id+"F28.imprint","IMPRINT",FACE,{"disambiguationData":[TD([[makeQuery(id+"F28.imprint","IMPRINT",EDGE,{"derivedFrom":sQuery(id+"F28.wireOp",EDGE,"E80.top")}),-1.0]])]});
            var Q1;
            {var subQ0=sQuery(id+"F28.wireOp",EDGE,"E90");Q1=makeQuery(id+"F28.imprint","IMPRINT",FACE,{"disambiguationData":[TD([[makeQuery(id+"F28.imprint","IMPRINT",EDGE,{"derivedFrom":subQ0}),1.0]])]});}
            var Q2;
            {var subQ0=sQuery(id+"F28.wireOp",EDGE,"E82");Q2=makeQuery(id+"F28.imprint","IMPRINT",FACE,{"disambiguationData":[TD([[makeQuery(id+"F28.imprint","IMPRINT",EDGE,{"derivedFrom":subQ0}),-1.0]])]});}
            var Q3;
            {var subQ3=sQuery(id+"F28.wireOp",EDGE,"E86");Q3=makeQuery(id+"F28.imprint","IMPRINT",FACE,{"disambiguationData":[TD([[makeQuery(id+"F28.imprint","IMPRINT",EDGE,{"derivedFrom":subQ3}),-1.0]])]});}
            var Q4;
            {var subQ20=sQuery(id+"F28.wireOp",EDGE,"E82");Q4=makeQuery(id+"F28.imprint","IMPRINT",FACE,{"disambiguationData":[TD([[makeQuery(id+"F28.imprint","IMPRINT",EDGE,{"derivedFrom":subQ20}),1.0]])]});}
            var Q5;
            {var subQ0=makeQuery(id+"F27.opExtrude","CAP_EDGE",EDGE,{"disambiguationData":[OSD([sQuery(id+"F21.wireOp",EDGE,"E57")])],"isStart":false});Q5=makeQuery(id+"F28.imprint","IMPRINT",FACE,{"disambiguationData":[TD([[makeQuery(id+"F28.imprint","IMPRINT",EDGE,{"derivedFrom":subQ0}),-1.0]])]});}
            var Q6;
            {var subQ5=makeQuery(id+"F27.opExtrude","CAP_EDGE",EDGE,{"disambiguationData":[OSD([sQuery(id+"F21.wireOp",EDGE,"E54")])],"isStart":false});Q6=makeQuery(id+"F28.imprint","IMPRINT",FACE,{"disambiguationData":[TD([[makeQuery(id+"F28.imprint","IMPRINT",EDGE,{"derivedFrom":subQ5}),-1.0]])]});}
            var Q7;
            Q7=makeQuery(id+"F28.imprint","IMPRINT",FACE,{"disambiguationData":[TD([[makeQuery(id+"F28.imprint","IMPRINT",EDGE,{"derivedFrom":makeQuery(id+"F27.opExtrude","CAP_EDGE",EDGE,{"disambiguationData":[OSD([sQuery(id+"F21.wireOp",EDGE,"E37")])],"isStart":false})}),1.0]])]});
            var Q8;
            {var subQ0=sQuery(id+"F28.wireOp",EDGE,"E80.bottom");var subQ1=makeQuery(id+"F27.opExtrude","CAP_EDGE",EDGE,{"disambiguationData":[OSD([sQuery(id+"F21.wireOp",EDGE,"E39")])],"isStart":false});var subQ2=makeQuery(id+"F28.imprint","INTERSECT",VERTEX,{"derivedFrom":[subQ1,subQ0]});var subQ3=makeQuery(id+"F27.opExtrude","CAP_EDGE",EDGE,{"disambiguationData":[OSD([sQuery(id+"F21.wireOp",EDGE,"E58")])],"isStart":false});var subQ4=makeQuery(id+"F28.imprint","INTERSECT",VERTEX,{"derivedFrom":[subQ3,subQ0]});Q8=makeQuery(id+"F28.imprint","IMPRINT",FACE,{"disambiguationData":[TD([[makeQuery(id+"F28.imprint","IMPRINT",EDGE,{"disambiguationData":[TD([[subQ2,-1.0],[subQ4,1.0]])],"derivedFrom":subQ0}),-1.0]])]});}
            var Q9;
            Q9=makeQuery(id+"F28.imprint","IMPRINT",FACE,{"disambiguationData":[TD([[makeQuery(id+"F28.imprint","IMPRINT",EDGE,{"derivedFrom":makeQuery(id+"F27.opExtrude","CAP_EDGE",EDGE,{"disambiguationData":[OSD([sQuery(id+"F21.wireOp",EDGE,"E36.0")])],"isStart":false})}),-1.0]])]});
            extrude(context, id + "F29", {"entities" : qUnion([Q0, Q1, Q2, Q3, Q4, Q5, Q6, Q7, Q8, Q9]), "depth" : getVariable(context, 'wt'), "offsetDistance" : 25 * mm});
        }
        {
            var Q0;
            {var subQ0=sQuery(id+"F28.wireOp",EDGE,"E90");Q0=makeQuery(id+"F28.imprint","IMPRINT",FACE,{"disambiguationData":[TD([[makeQuery(id+"F28.imprint","IMPRINT",EDGE,{"derivedFrom":subQ0}),1.0]])]});}
            var Q1;
            {var subQ3=sQuery(id+"F28.wireOp",EDGE,"E86");Q1=makeQuery(id+"F28.imprint","IMPRINT",FACE,{"disambiguationData":[TD([[makeQuery(id+"F28.imprint","IMPRINT",EDGE,{"derivedFrom":subQ3}),-1.0]])]});}
            var Q2;
            {var subQ0=sQuery(id+"F28.wireOp",EDGE,"E82");Q2=makeQuery(id+"F28.imprint","IMPRINT",FACE,{"disambiguationData":[TD([[makeQuery(id+"F28.imprint","IMPRINT",EDGE,{"derivedFrom":subQ0}),-1.0]])]});}
            extrude(context, id + "F30", {"entities" : qUnion([Q0, Q1, Q2]), "operationType" : NewBodyOperationType.ADD, "oppositeDirection" : true, "depth" : 10 * mm, "offsetDistance" : 25 * mm});
        }
        {
            var Q0;
            {var subQ0=sQuery(id+"F21.wireOp",EDGE,"E33");Q0=makeQuery(id+"F27.boolean.opBoolean","MERGE",FACE,{"derivedFrom":[makeQuery(id+"F22.opExtrude","SWEPT_FACE",FACE,{"disambiguationData":[OSD([subQ0])]}),makeQuery(id+"F27.opExtrude","SWEPT_FACE",FACE,{"disambiguationData":[OSD([subQ0])]})]});}
            var sketch = newSketch(context, id + "F31", { "sketchPlane" : qUnion([Q0])});
            skCircle(sketch, "E96", {"center": v(-95, 9) * mm, "radius": 4.5 * mm});
            skCircle(sketch, "E97.0.1.0", {"center": v(-95, 24) * mm, "radius": 4.5 * mm});
            skLineSegment(sketch, "E97.direction1", {"start": v(-95, 9) * mm, "end": v(-74, 9) * mm, "construction": true});
            skLineSegment(sketch, "E97.direction2", {"start": v(-95, 9) * mm, "end": v(-95, 24) * mm, "construction": true});
            skCircle(sketch, "E98", {"center": v(-95, 36) * mm, "radius": 2.5 * mm});
            skSolve(sketch);
        }
        {
            var Q0;
            Q0=makeQuery(id+"F31.imprint","IMPRINT",FACE,{"disambiguationData":[TD([[makeQuery(id+"F31.imprint","IMPRINT",EDGE,{"derivedFrom":sQuery(id+"F31.wireOp",EDGE,"E98")}),1.0]])]});
            var Q1;
            Q1=makeQuery(id+"F31.imprint","IMPRINT",FACE,{"disambiguationData":[TD([[makeQuery(id+"F31.imprint","IMPRINT",EDGE,{"derivedFrom":sQuery(id+"F31.wireOp",EDGE,"E97.0.1.0")}),1.0]])]});
            var Q2;
            Q2=makeQuery(id+"F31.imprint","IMPRINT",FACE,{"disambiguationData":[TD([[makeQuery(id+"F31.imprint","IMPRINT",EDGE,{"derivedFrom":sQuery(id+"F31.wireOp",EDGE,"E96")}),1.0]])]});
            var Q3;
            Q3=makeQuery(id+"F27.opExtrude","SWEPT_FACE",FACE,{"disambiguationData":[OSD([sQuery(id+"F21.wireOp",EDGE,"E36.1")])]});
            extrude(context, id + "F32", {"entities" : qUnion([Q0, Q1, Q2]), "operationType" : NewBodyOperationType.REMOVE, "endBound" : BoundingType.UP_TO_SURFACE, "oppositeDirection" : true, "depth" : 25 * mm, "endBoundEntityFace" : qUnion([Q3]), "offsetDistance" : 25 * mm});
        }
    });
